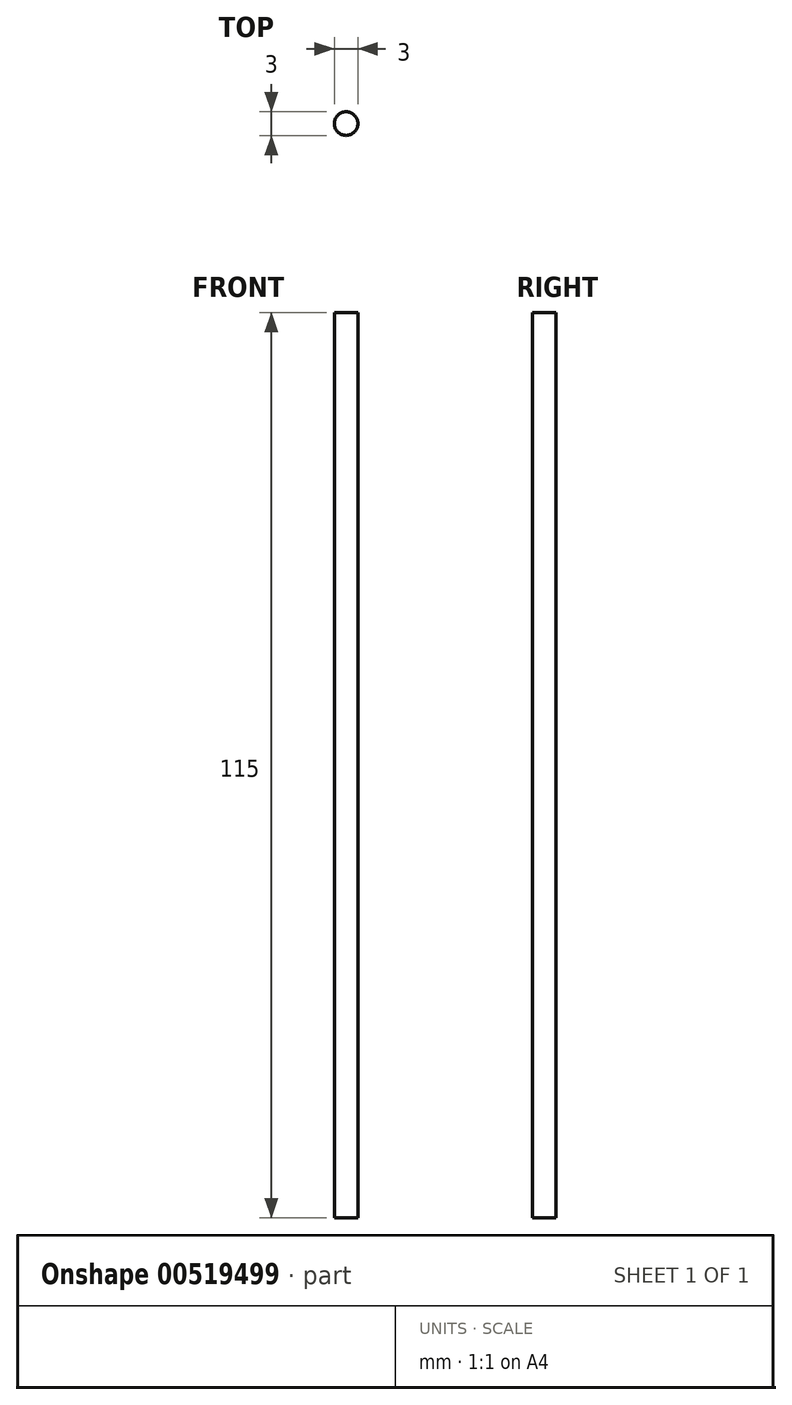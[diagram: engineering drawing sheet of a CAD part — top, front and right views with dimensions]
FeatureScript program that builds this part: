
annotation { "Feature Type Name" : "Feature", "Feature Type Description" : "" }
export const myFeature = defineFeature(function(context is Context, id is Id, definition is map)
    precondition{}
    {
        {
            var Q0;
            Q0=qCreatedBy(makeId("Top.planeOp"),FACE);
            var sketch = newSketch(context, id + "F0", { "sketchPlane" : qUnion([Q0])});
            skCircle(sketch, "E0", {"center": v(0, 0) * mm, "radius": 1.5 * mm});
            skSolve(sketch);
        }
        {
            var Q0;
            Q0=makeQuery(id+"F0.imprint","IMPRINT",FACE,{"disambiguationData":[TD([[makeQuery(id+"F0.imprint","IMPRINT",EDGE,{"derivedFrom":sQuery(id+"F0.wireOp",EDGE,"E0")}),1.0]])]});
            extrude(context, id + "F1", {"entities" : qUnion([Q0]), "depth" : 115 * mm, "offsetDistance" : 25 * mm});
        }
    });
